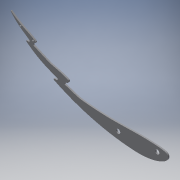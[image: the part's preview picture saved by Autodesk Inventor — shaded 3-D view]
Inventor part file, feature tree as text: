
AUTODESK INVENTOR PART (.ipt)
format: ipt  version: 2018 (Build 220112000, 112)  size: 189,952 bytes
history: native  units: mm
features: extrude x2, sketch x2
ambient origin geometry x8: Origin, YZ Plane, XZ Plane, XY Plane, X Axis, Y Axis, Z Axis, Center Point
bodies: Body1 (feature_tree)
feature tree (4):
  extrude  "押し出し2"  Depth=4.0mm
  extrude  "押し出し3"  Depth=4.0mm TaperAngle=0.0deg
  sketch  "スケッチ1"
  sketch  "スケッチ2"
